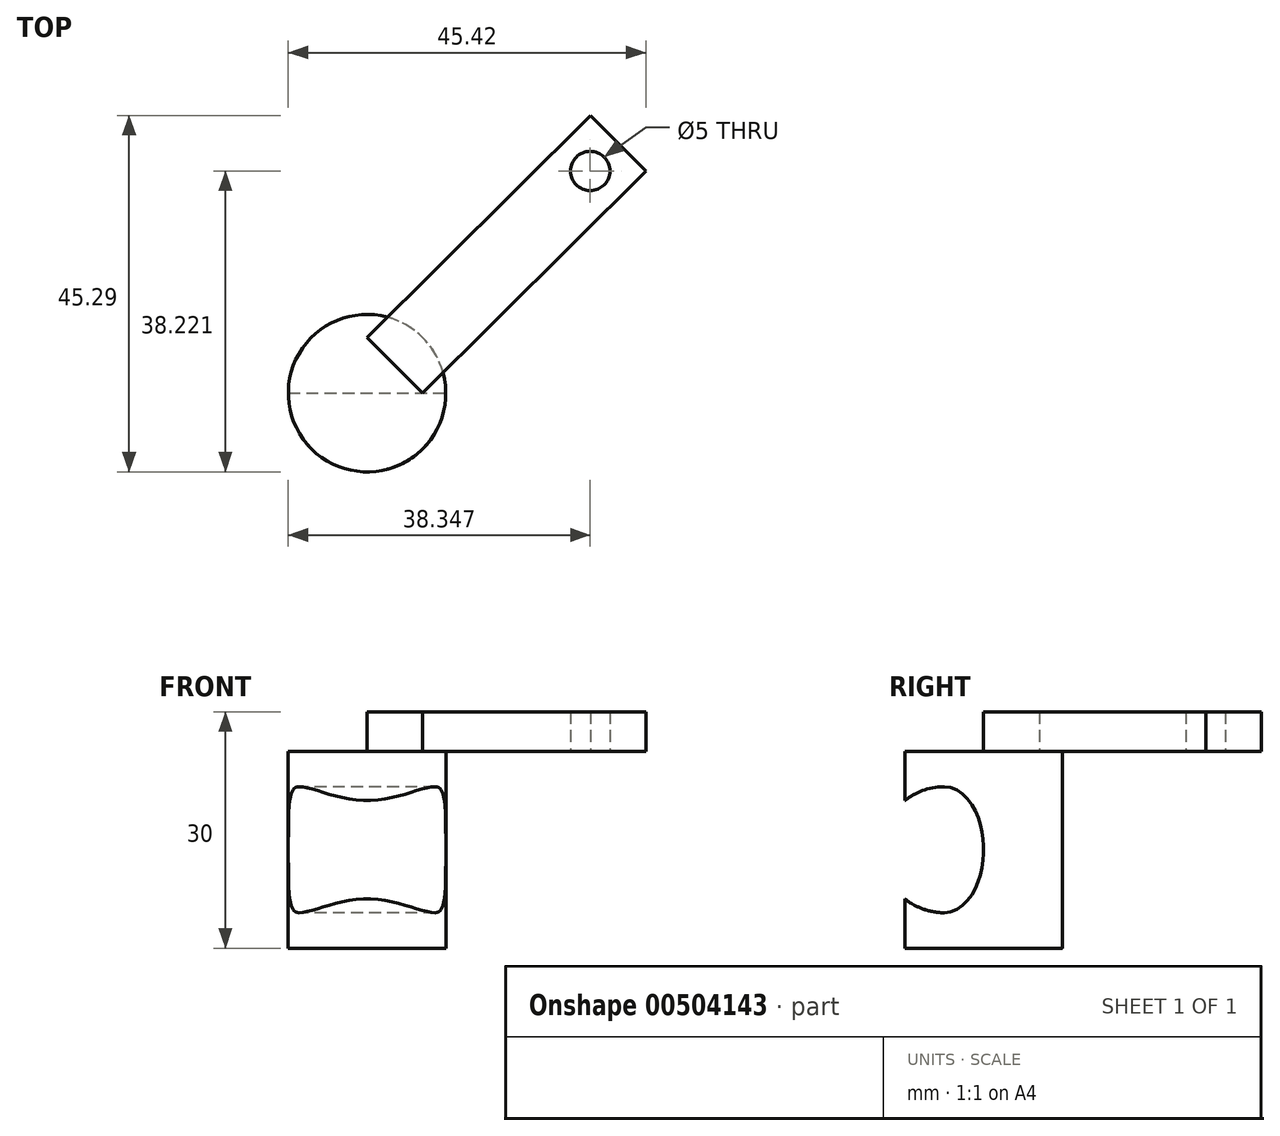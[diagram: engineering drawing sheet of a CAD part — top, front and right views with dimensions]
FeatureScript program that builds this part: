
annotation { "Feature Type Name" : "Feature", "Feature Type Description" : "" }
export const myFeature = defineFeature(function(context is Context, id is Id, definition is map)
    precondition{}
    {
        {
            var Q0;
            Q0=qCreatedBy(makeId("Top.planeOp"),FACE);
            var sketch = newSketch(context, id + "F0", { "sketchPlane" : qUnion([Q0])});
            skCircle(sketch, "E0", {"center": v(0, 0) * mm, "radius": 10 * mm});
            skSolve(sketch);
        }
        {
            var Q0;
            Q0 = qSketchRegion(id + "F0", true);
            extrude(context, id + "F1", {"entities" : qUnion([Q0]), "depth" : 25 * mm, "offsetDistance" : 25 * mm});
        }
        {
            var Q0;
            Q0=qCreatedBy(makeId("Right.planeOp"),FACE);
            var sketch = newSketch(context, id + "F2", { "sketchPlane" : qUnion([Q0])});
            skEllipse(sketch, "E1", {"center": v(-5, 12.5) * mm, "majorRadius": 8 * mm, "minorRadius": 5 * mm, "majorAxis": v(0, 1)});
            skArc(sketch, "E2", {"start": v(-5, 20.5) * mm, "mid": v(-13, 12.5) * mm, "end": v(-5, 4.5) * mm});
            skSolve(sketch);
        }
        {
            var Q0;
            {var subQ0=sQuery(id+"F2.wireOp",EDGE,"E2");var subQ1=sQuery(id+"F2.wireOp",EDGE,"E1");var subQ2=makeQuery(id+"F2.imprint","INTERSECT",VERTEX,{"disambiguationData":[OD(0.0)],"derivedFrom":[subQ1,subQ0]});Q0=makeQuery(id+"F2.imprint","IMPRINT",FACE,{"disambiguationData":[TD([[makeQuery(id+"F2.imprint","IMPRINT",EDGE,{"disambiguationData":[TD([[subQ2,-1.0]])],"derivedFrom":subQ1}),1.0]])]});}
            var Q1;
            {var subQ0=sQuery(id+"F2.wireOp",EDGE,"E2");Q1=makeQuery(id+"F2.imprint","IMPRINT",FACE,{"disambiguationData":[TD([[makeQuery(id+"F2.imprint","IMPRINT",EDGE,{"derivedFrom":subQ0}),1.0]])]});}
            extrude(context, id + "F3", {"entities" : qUnion([Q0, Q1]), "operationType" : NewBodyOperationType.REMOVE, "endBound" : BoundingType.SYMMETRIC, "depth" : 25 * mm, "offsetDistance" : 25 * mm});
        }
        {
            var Q0;
            Q0=makeQuery(id+"F1.opExtrude","CAP_FACE",FACE,{"disambiguationData":[OSD([sQuery(id+"F0.wireOp",EDGE,"E0")])],"isStart":false});
            var sketch = newSketch(context, id + "F4", { "sketchPlane" : qUnion([Q0])});
            skLineSegment(sketch, "E3", {"start": v(0, 7.1) * mm, "end": v(7.05, 0) * mm});
            skLineSegment(sketch, "E4", {"start": v(7.05, 0) * mm, "end": v(35.42, 28.2) * mm});
            skLineSegment(sketch, "E5", {"start": v(35.42, 28.2) * mm, "end": v(28.37, 35.3) * mm});
            skLineSegment(sketch, "E6", {"start": v(28.37, 35.3) * mm, "end": v(0, 7.1) * mm});
            skCircle(sketch, "E7", {"center": v(28.35, 28.22) * mm, "radius": 2.5 * mm});
            skSolve(sketch);
        }
        {
            var Q0;
            Q0 = qSketchRegion(id + "F4", true);
            extrude(context, id + "F5", {"entities" : qUnion([Q0]), "operationType" : NewBodyOperationType.ADD, "depth" : 5 * mm, "offsetDistance" : 25 * mm});
        }
    });
